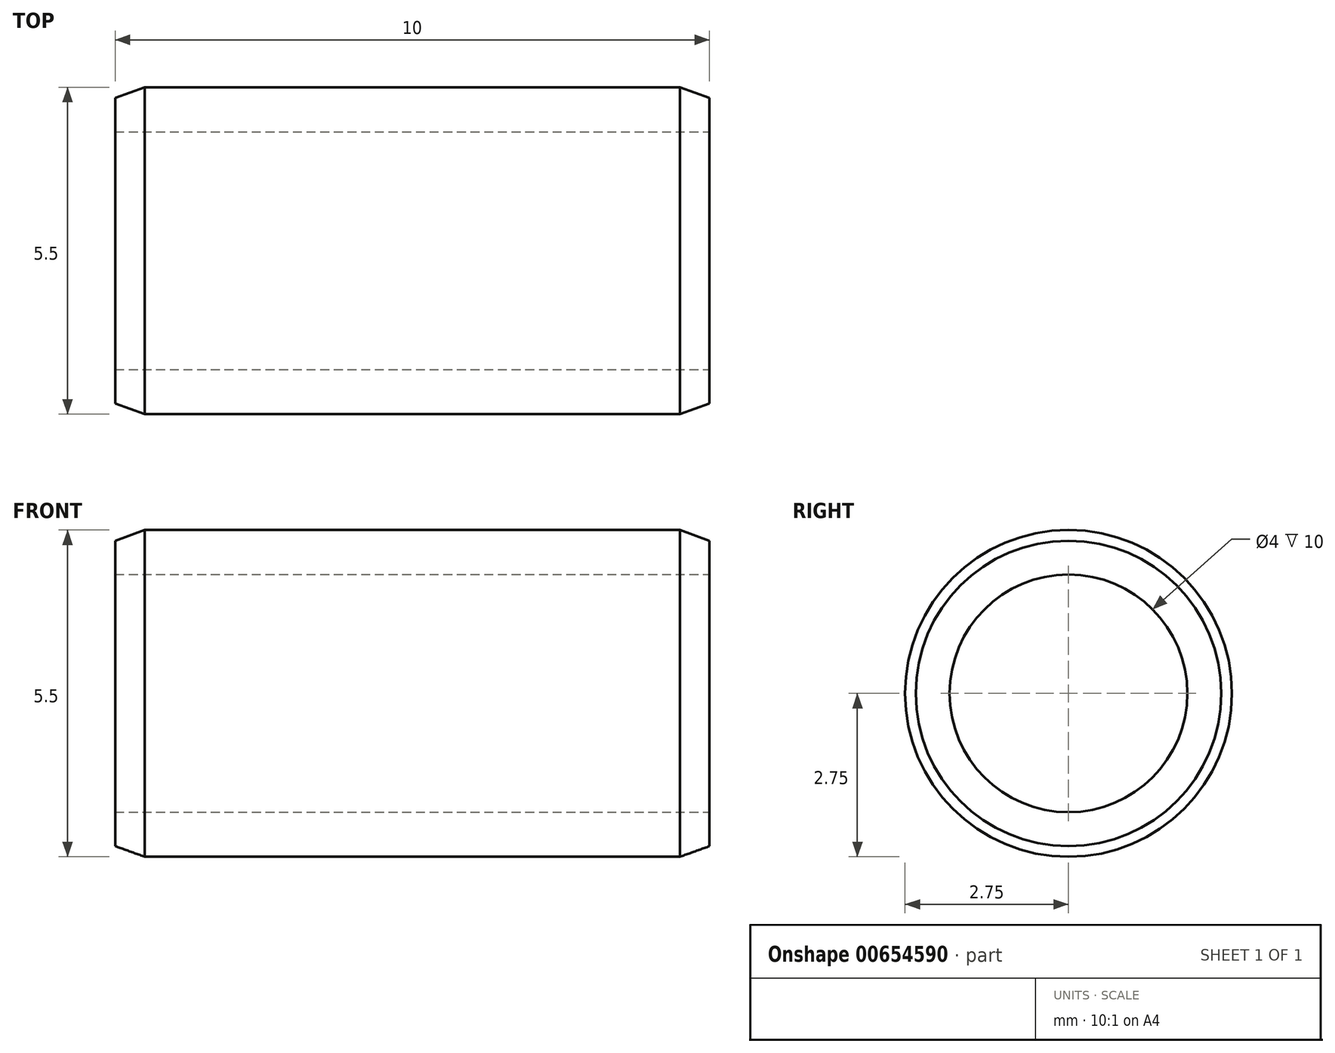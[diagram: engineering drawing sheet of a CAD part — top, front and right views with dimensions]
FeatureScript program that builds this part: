
annotation { "Feature Type Name" : "Feature", "Feature Type Description" : "" }
export const myFeature = defineFeature(function(context is Context, id is Id, definition is map)
    precondition{}
    {
        {
            var Q0;
            Q0=qCreatedBy(makeId("Front.planeOp"),FACE);
            var sketch = newSketch(context, id + "F0", { "sketchPlane" : qUnion([Q0])});
            skLineSegment(sketch, "E0", {"start": v(-5, 0) * mm, "end": v(-5, 2.57) * mm});
            skLineSegment(sketch, "E1", {"start": v(-5, 2.57) * mm, "end": v(-4.5, 2.75) * mm});
            skLineSegment(sketch, "E2", {"start": v(-4.5, 2.75) * mm, "end": v(4.5, 2.75) * mm});
            skLineSegment(sketch, "E3", {"start": v(4.5, 2.75) * mm, "end": v(5, 2.57) * mm});
            skLineSegment(sketch, "E4", {"start": v(5, 2.57) * mm, "end": v(5, 0) * mm});
            skLineSegment(sketch, "E5", {"start": v(5, 0) * mm, "end": v(0, 0) * mm});
            skLineSegment(sketch, "E6", {"start": v(0, 0) * mm, "end": v(-5, 0) * mm});
            skSolve(sketch);
        }
        {
            var Q0;
            Q0=makeQuery(id+"F0.imprint","IMPRINT",FACE,{"disambiguationData":[TD([[makeQuery(id+"F0.imprint","IMPRINT",EDGE,{"derivedFrom":sQuery(id+"F0.wireOp",EDGE,"E0")}),-1.0]])]});
            var Q1;
            Q1=sQuery(id+"F0.wireOp",EDGE,"E6");
            revolve(context, id + "F1", {"surfaceOperationType" : NewSurfaceOperationType.NEW, "entities" : qUnion([Q0]), "axis" : qUnion([Q1]), "revolveType" : RevolveType.FULL});
        }
        {
            var Q0;
            Q0=makeQuery(id+"F1.opRevolve","SWEPT_FACE",FACE,{"disambiguationData":[OSD([sQuery(id+"F0.wireOp",EDGE,"E4")])]});
            var sketch = newSketch(context, id + "F2", { "sketchPlane" : qUnion([Q0])});
            skCircle(sketch, "E7", {"center": v(0, 0) * mm, "radius": 2 * mm});
            skSolve(sketch);
        }
        {
            var Q0;
            Q0=makeQuery(id+"F2.imprint","IMPRINT",FACE,{"disambiguationData":[TD([[makeQuery(id+"F2.imprint","IMPRINT",EDGE,{"derivedFrom":sQuery(id+"F2.wireOp",EDGE,"E7")}),1.0]])]});
            extrude(context, id + "F3", {"entities" : qUnion([Q0]), "operationType" : NewBodyOperationType.REMOVE, "endBound" : BoundingType.UP_TO_NEXT, "oppositeDirection" : true, "depth" : 25 * mm, "offsetDistance" : 25 * mm});
        }
    });
